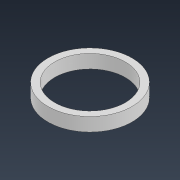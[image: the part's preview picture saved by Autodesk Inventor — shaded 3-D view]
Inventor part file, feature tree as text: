
AUTODESK INVENTOR PART (.ipt)
format: ipt  version: 2022 (Build 260153000, 153)  size: 83,456 bytes
history: native  units: mm
features: extrude x1, sketch x1
ambient origin geometry x8: Origin, YZ Plane, XZ Plane, XY Plane, X Axis, Y Axis, Z Axis, Center Point
bodies: Solid1 (feature_tree)
feature tree (2):
  extrude  "Extrusion1"  Depth=8.0mm
  sketch  "Sketch1"  dims[d0=42.0mm d1=50.0mm d2=8.0mm d3=0.0mm]
